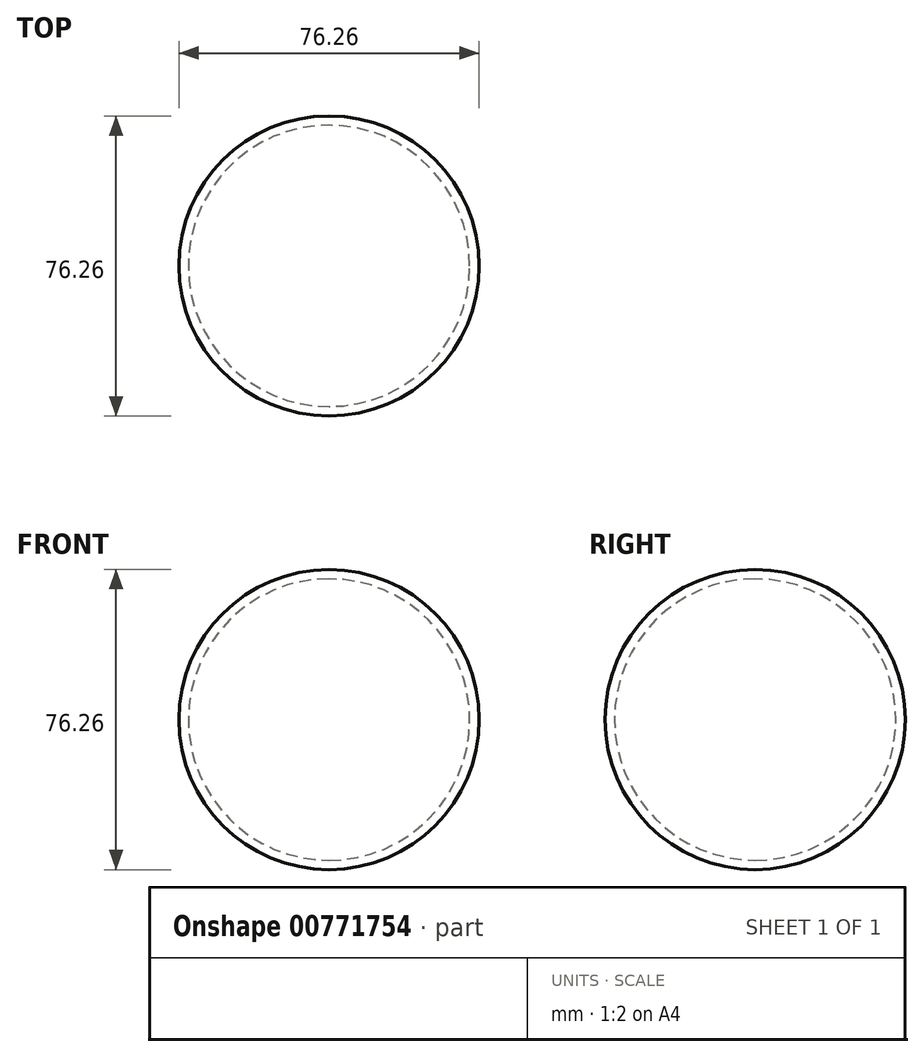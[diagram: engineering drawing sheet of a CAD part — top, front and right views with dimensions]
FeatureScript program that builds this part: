
annotation { "Feature Type Name" : "Feature", "Feature Type Description" : "" }
export const myFeature = defineFeature(function(context is Context, id is Id, definition is map)
    precondition{}
    {
        {
            var Q0;
            Q0=qCreatedBy(makeId("Front.planeOp"),FACE);
            var sketch = newSketch(context, id + "F0", { "sketchPlane" : qUnion([Q0])});
            skArc(sketch, "E0", {"start": v(0, 38.13) * mm, "mid": v(-38.13, 0) * mm, "end": v(0, -38.13) * mm});
            skArc(sketch, "E1", {"start": v(0, 35.74) * mm, "mid": v(-35.74, 0) * mm, "end": v(0, -35.74) * mm});
            skLineSegment(sketch, "E2", {"start": v(0, 35.74) * mm, "end": v(0, 38.13) * mm});
            skLineSegment(sketch, "E3", {"start": v(0, -35.74) * mm, "end": v(0, -38.13) * mm});
            skSolve(sketch);
        }
        {
            var Q0;
            Q0=qCreatedBy(makeId("Front.planeOp"),FACE);
            var sketch = newSketch(context, id + "F1", { "sketchPlane" : qUnion([Q0])});
            skLineSegment(sketch, "E4", {"start": v(0, 38.3) * mm, "end": v(0, -38.5) * mm});
            skSolve(sketch);
        }
        {
            var Q0;
            Q0=makeQuery(id+"F0.imprint","IMPRINT",FACE,{"disambiguationData":[TD([[makeQuery(id+"F0.imprint","IMPRINT",EDGE,{"derivedFrom":sQuery(id+"F0.wireOp",EDGE,"E0")}),1.0]])]});
            var Q1;
            Q1=sQuery(id+"F1.wireOp",EDGE,"E4");
            revolve(context, id + "F2", {"surfaceOperationType" : NewSurfaceOperationType.NEW, "entities" : qUnion([Q0]), "axis" : qUnion([Q1]), "revolveType" : RevolveType.FULL});
        }
    });
